# Revit family: SC_КронштейнНапольный_КНZ7_Steelcap
name_source: partatom
category: Оборудование
units: mm (PartAtom-declared; Revit-internal decimal feet)

## family parameters
Всегда вертикально = Да
На основе рабочей плоскости = Нет
Общий = Нет
При загрузке вырезать с полостями = Нет
Размер круглого соединителя = Использовать диаметр
Сохранять ориентацию аннотаций = Нет
Тип детали = Нормальный
Точка принадлежности помещению = Нет

## types (2) — shared parameters
ADSK_URL страницы изделия = https://kronshtein.ru
ADSK_Версия Revit = Revit 2026
ADSK_Единица измерения = шт.
ADSK_Завод-изготовитель = ООО "Стилкэп"
ADSK_Код изделия = KНZ7
ADSK_Марка = KНZ7
ADSK_Материал = Белый
ADSK_Наименование = Кронштейн напольный
ADSK_Наименование краткое = Кронштейн напольный
DSI_Артикул по каталогу = KНZ7
DSI_Производитель = Steelcap
URL = https://kronshtein.ru
Изготовитель = Steelcap
Ключевая пометка = ﻿﻿  ﻿          ​     ​                                      ﻿       ﻿ ﻿         ​     ​ ﻿                                  ​  ​  ​  ​    ​  ​    ​        ﻿﻿
Комментарии к типоразмеру = ﻿﻿  ﻿          ​     ​                                      ﻿       ﻿ ﻿         ​     ​ ﻿                                  ​  ​  ​  ​    ​  ​    ​        ﻿﻿
Модель = Напольные кронштейны
Производитель_Контакты = +7 922 995-00-70
расстояние до нижнего ползуна = 150 мм
zero-valued in all types: ADSK_Масса, Отметка по умолчанию, снятие крышки

## per-type parameters (varying)
| type | Высота | Код по классификатору | Описание | видимость крышки | высота верхнего ползуна от нижнего |
| Кронштейн_Напольный_КНZ7.70 | 700 мм | ﻿﻿ | h=500 | Да | 500 мм |
| Кронштейн_Напольный_KНZ7.50 | 500 мм |  | h=300 | Нет | 300 мм |

## geometry (parser evidence)
native form markers: Blend x4
no freeform markers — native parametric forms only
